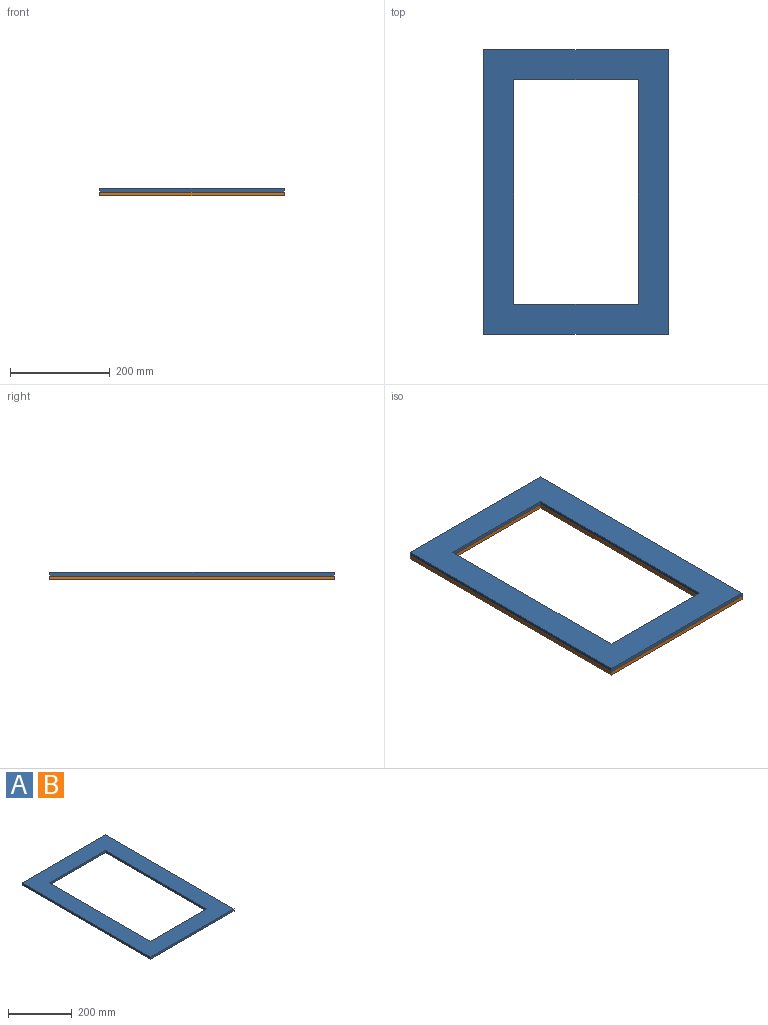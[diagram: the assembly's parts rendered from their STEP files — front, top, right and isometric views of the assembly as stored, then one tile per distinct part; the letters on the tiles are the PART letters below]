
ASSEMBLY  parts=2 mates=1
PART A: 10 faces, bbox 370x570x8 mm
  f0: plane 250x8mm, normal (0,-1,0), area 2000mm2, adj f1,f7,f8,f9
  f1: plane 450x8mm, normal (-1,0,0), area 3600mm2, adj f0,f2,f8,f9
  f2: plane 250x8mm, normal (0,1,0), area 2000mm2, adj f1,f7,f8,f9
  f3: plane 370x8mm, normal (0,-1,0), area 2960mm2, adj f4,f6,f8,f9
  f4: plane 570x8mm, normal (1,0,0), area 4560mm2, adj f3,f5,f8,f9
  f5: plane 370x8mm, normal (0,1,0), area 2960mm2, adj f4,f6,f8,f9
  f6: plane 570x8mm, normal (-1,0,0), area 4560mm2, adj f3,f5,f8,f9
  f7: plane 450x8mm, normal (1,0,0), area 3600mm2, adj f0,f2,f8,f9
  f8: plane 570x370mm, normal (0,0,1), area 98400mm2, adj f0,f1,f2,f3,f4,f5,f6,f7
  f9: plane 570x370mm, normal (0,0,-1), area 98400mm2, adj f0,f1,f2,f3,f4,f5,f6,f7
PART B: same geometry as A
PLACE A t=(-142.86,-62.25,26.35)mm
PLACE B t=(-142.86,-62.25,18.35)mm
MATE fastened B.f8 <-> A.f9  axis (0,0,1) through (-142.86,-62.25,26.35)mm
